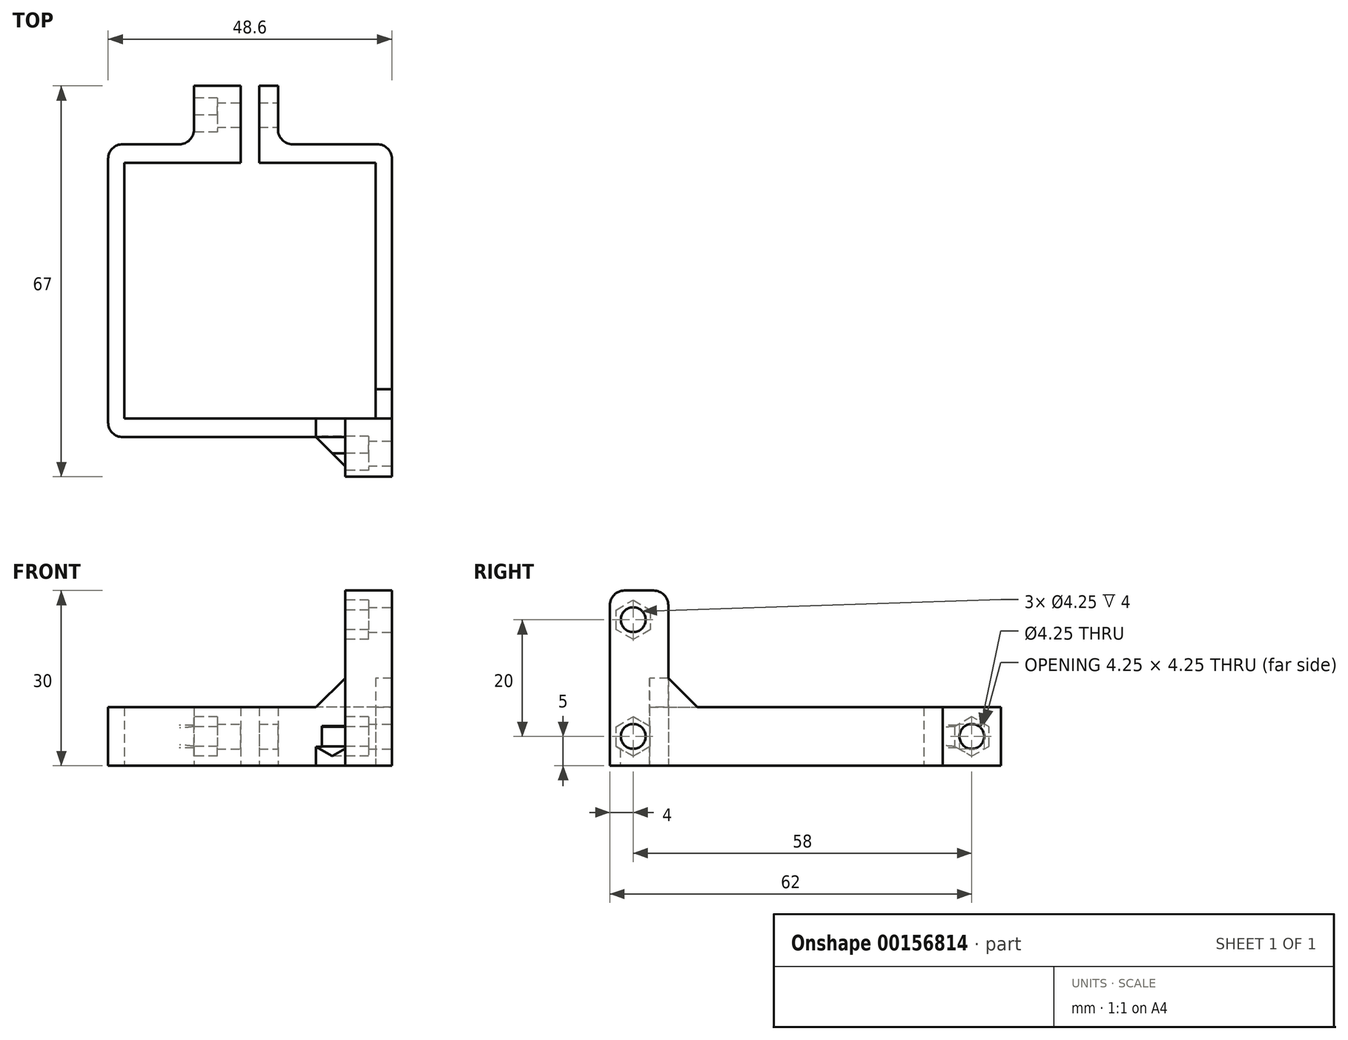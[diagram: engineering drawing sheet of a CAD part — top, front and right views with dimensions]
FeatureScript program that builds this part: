
annotation { "Feature Type Name" : "Feature", "Feature Type Description" : "" }
export const myFeature = defineFeature(function(context is Context, id is Id, definition is map)
    precondition{}
    {
        {
            var Q0;
            Q0=qCreatedBy(makeId("Top.planeOp"),FACE);
            var sketch = newSketch(context, id + "F0", { "sketchPlane" : qUnion([Q0])});
            skLineSegment(sketch, "E0.bottom", {"start": v(21.1, -21.1) * mm, "end": v(-21.1, -21.1) * mm, "construction": true});
            skLineSegment(sketch, "E0.top", {"start": v(21.1, 21.1) * mm, "end": v(-21.1, 21.1) * mm, "construction": true});
            skLineSegment(sketch, "E0.left", {"start": v(21.1, -21.1) * mm, "end": v(21.1, 21.1) * mm, "construction": true});
            skLineSegment(sketch, "E0.right", {"start": v(-21.1, -21.1) * mm, "end": v(-21.1, 21.1) * mm, "construction": true});
            skPoint(sketch, "E0.middle", {"position": v(0, 0) * mm});
            skLineSegment(sketch, "E1.bottom", {"start": v(21.5, -21.9) * mm, "end": v(-21.5, -21.9) * mm});
            skLineSegment(sketch, "E1.top", {"start": v(21.5, 21.9) * mm, "end": v(1.6, 21.9) * mm});
            skLineSegment(sketch, "E1.left", {"start": v(21.5, -21.9) * mm, "end": v(21.5, 21.9) * mm});
            skLineSegment(sketch, "E1.right", {"start": v(-21.5, -21.9) * mm, "end": v(-21.5, 21.9) * mm});
            skLineSegment(sketch, "E2.bottom", {"start": v(24.3, -25.1) * mm, "end": v(-24.3, -25.1) * mm});
            skLineSegment(sketch, "E2.top", {"start": v(24.3, 25.1) * mm, "end": v(4.8, 25.1) * mm});
            skLineSegment(sketch, "E2.left", {"start": v(24.3, -25.1) * mm, "end": v(24.3, 25.1) * mm});
            skLineSegment(sketch, "E2.right", {"start": v(-24.3, -25.1) * mm, "end": v(-24.3, 25.1) * mm});
            skLineSegment(sketch, "E3", {"start": v(-9.6, 25.1) * mm, "end": v(-9.6, 35.1) * mm});
            skLineSegment(sketch, "E4", {"start": v(-9.6, 35.1) * mm, "end": v(-1.6, 35.1) * mm});
            skLineSegment(sketch, "E5", {"start": v(-1.6, 35.1) * mm, "end": v(-1.6, 21.9) * mm});
            skLineSegment(sketch, "E6", {"start": v(1.6, 21.9) * mm, "end": v(1.6, 35.1) * mm});
            skLineSegment(sketch, "E7", {"start": v(1.6, 35.1) * mm, "end": v(4.8, 35.1) * mm});
            skLineSegment(sketch, "E8", {"start": v(4.8, 35.1) * mm, "end": v(4.8, 25.1) * mm});
            skLineSegment(sketch, "E9.trimOffspring", {"start": v(-9.6, 25.1) * mm, "end": v(-24.3, 25.1) * mm});
            skLineSegment(sketch, "E10.trimOffspring", {"start": v(-1.6, 21.9) * mm, "end": v(-21.5, 21.9) * mm});
            skSolve(sketch);
        }
        {
            var Q0;
            Q0=qSketchRegion(id+"F0",true);
            extrude(context, id + "F1", {"entities" : qUnion([Q0]), "depth" : 10 * mm});
        }
        {
            var Q0;
            Q0=makeQuery(id+"F1.opExtrude","SWEPT_FACE",FACE,{"disambiguationData":[OSD([sQuery(id+"F0.wireOp",EDGE,"E8")])]});
            var sketch = newSketch(context, id + "F2", { "sketchPlane" : qUnion([Q0])});
            skCircle(sketch, "E11", {"center": v(30.1, 5) * mm, "radius": 2.12 * mm});
            skSolve(sketch);
        }
        {
            var Q0;
            Q0=qSketchRegion(id+"F2",true);
            extrude(context, id + "F3", {"entities" : qUnion([Q0]), "operationType" : NewBodyOperationType.REMOVE, "endBound" : BoundingType.THROUGH_ALL, "oppositeDirection" : true, "depth" : 25 * mm});
        }
        {
            var Q0;
            Q0=qCreatedBy(makeId("Top.planeOp"),FACE);
            var sketch = newSketch(context, id + "F4", { "sketchPlane" : qUnion([Q0])});
            skLineSegment(sketch, "E12.bottom", {"start": v(16.3, -21.9) * mm, "end": v(24.3, -21.9) * mm});
            skLineSegment(sketch, "E12.top", {"start": v(16.3, -31.9) * mm, "end": v(24.3, -31.9) * mm});
            skLineSegment(sketch, "E12.left", {"start": v(16.3, -21.9) * mm, "end": v(16.3, -31.9) * mm});
            skLineSegment(sketch, "E12.right", {"start": v(24.3, -21.9) * mm, "end": v(24.3, -31.9) * mm});
            skLineSegment(sketch, "E13.bottom", {"start": v(-24.3, 21.9) * mm, "end": v(-14.3, 21.9) * mm, "construction": true});
            skLineSegment(sketch, "E13.top", {"start": v(-24.3, 29.9) * mm, "end": v(-14.3, 29.9) * mm, "construction": true});
            skLineSegment(sketch, "E13.left", {"start": v(-24.3, 21.9) * mm, "end": v(-24.3, 29.9) * mm, "construction": true});
            skLineSegment(sketch, "E13.right", {"start": v(-14.3, 21.9) * mm, "end": v(-14.3, 29.9) * mm, "construction": true});
            skSolve(sketch);
        }
        {
            var Q0;
            Q0=qSketchRegion(id+"F4",true);
            extrude(context, id + "F5", {"entities" : qUnion([Q0]), "operationType" : NewBodyOperationType.ADD, "depth" : 30 * mm});
        }
        {
            var Q0;
            Q0=makeQuery(id+"F5.boolean.opBoolean","MERGE",FACE,{"derivedFrom":[makeQuery(id+"F1.opExtrude","SWEPT_FACE",FACE,{"disambiguationData":[OSD([sQuery(id+"F0.wireOp",EDGE,"E2.left")])]}),makeQuery(id+"F5.opExtrude","SWEPT_FACE",FACE,{"disambiguationData":[OSD([sQuery(id+"F4.wireOp",EDGE,"E12.right")])]})]});
            var sketch = newSketch(context, id + "F6", { "sketchPlane" : qUnion([Q0])});
            skCircle(sketch, "E14", {"center": v(-27.9, 25) * mm, "radius": 2.12 * mm});
            skCircle(sketch, "E15", {"center": v(-27.9, 5) * mm, "radius": 2.12 * mm});
            skSolve(sketch);
        }
        {
            var Q0;
            Q0=qSketchRegion(id+"F6",true);
            extrude(context, id + "F7", {"entities" : qUnion([Q0]), "operationType" : NewBodyOperationType.REMOVE, "endBound" : BoundingType.THROUGH_ALL, "oppositeDirection" : true, "depth" : 25 * mm});
        }
        {
            var Q0;
            Q0=makeQuery(id+"F5.opExtrude","SWEPT_FACE",FACE,{"disambiguationData":[OSD([sQuery(id+"F4.wireOp",EDGE,"E12.left")])]});
            var sketch = newSketch(context, id + "F8", { "sketchPlane" : qUnion([Q0])});
            skCircle(sketch, "E16.cCircle", {"center": v(27.9, 25) * mm, "radius": 2.93 * mm, "construction": true});
            skLineSegment(sketch, "E16.0", {"start": v(30.82, 26.69) * mm, "end": v(30.82, 23.31) * mm});
            skLineSegment(sketch, "E16.1", {"start": v(30.82, 23.31) * mm, "end": v(27.9, 21.62) * mm});
            skLineSegment(sketch, "E16.2", {"start": v(27.9, 21.62) * mm, "end": v(24.98, 23.31) * mm});
            skLineSegment(sketch, "E16.3", {"start": v(24.97, 23.31) * mm, "end": v(24.97, 26.69) * mm});
            skLineSegment(sketch, "E16.4", {"start": v(24.98, 26.69) * mm, "end": v(27.9, 28.38) * mm});
            skLineSegment(sketch, "E16.5", {"start": v(27.9, 28.38) * mm, "end": v(30.82, 26.69) * mm});
            skPoint(sketch, "E16.0.midPoint", {"position": v(30.82, 25) * mm});
            skCircle(sketch, "E17.cCircle", {"center": v(27.9, 5) * mm, "radius": 2.93 * mm, "construction": true});
            skLineSegment(sketch, "E17.0", {"start": v(30.82, 6.69) * mm, "end": v(30.82, 3.31) * mm});
            skLineSegment(sketch, "E17.1", {"start": v(30.83, 3.31) * mm, "end": v(27.9, 1.62) * mm});
            skLineSegment(sketch, "E17.2", {"start": v(27.9, 1.62) * mm, "end": v(24.98, 3.31) * mm});
            skLineSegment(sketch, "E17.3", {"start": v(24.97, 3.31) * mm, "end": v(24.97, 6.69) * mm});
            skLineSegment(sketch, "E17.4", {"start": v(24.97, 6.69) * mm, "end": v(27.9, 8.38) * mm});
            skLineSegment(sketch, "E17.5", {"start": v(27.9, 8.38) * mm, "end": v(30.82, 6.69) * mm});
            skPoint(sketch, "E17.0.midPoint", {"position": v(30.82, 5) * mm});
            skSolve(sketch);
        }
        {
            var Q0;
            Q0=qSketchRegion(id+"F8",true);
            extrude(context, id + "F9", {"entities" : qUnion([Q0]), "operationType" : NewBodyOperationType.REMOVE, "endBound" : BoundingType.SYMMETRIC, "oppositeDirection" : true, "depth" : 8 * mm});
        }
        {
            var Q0;
            Q0=makeQuery(id+"F5.boolean.opBoolean","INTERSECT",EDGE,{"derivedFrom":[makeQuery(id+"F1.opExtrude","CAP_FACE",FACE,{"disambiguationData":[OSD([sQuery(id+"F0.wireOp",EDGE,"E1.bottom"),sQuery(id+"F0.wireOp",EDGE,"E1.top"),sQuery(id+"F0.wireOp",EDGE,"E1.left"),sQuery(id+"F0.wireOp",EDGE,"E1.right"),sQuery(id+"F0.wireOp",EDGE,"E2.bottom"),sQuery(id+"F0.wireOp",EDGE,"E2.top"),sQuery(id+"F0.wireOp",EDGE,"E2.left"),sQuery(id+"F0.wireOp",EDGE,"E2.right"),sQuery(id+"F0.wireOp",EDGE,"E3"),sQuery(id+"F0.wireOp",EDGE,"E4"),sQuery(id+"F0.wireOp",EDGE,"E5"),sQuery(id+"F0.wireOp",EDGE,"E6"),sQuery(id+"F0.wireOp",EDGE,"E7"),sQuery(id+"F0.wireOp",EDGE,"E8"),sQuery(id+"F0.wireOp",EDGE,"E9.trimOffspring"),sQuery(id+"F0.wireOp",EDGE,"E10.trimOffspring")])],"isStart":false}),makeQuery(id+"F5.opExtrude","SWEPT_FACE",FACE,{"disambiguationData":[OSD([sQuery(id+"F4.wireOp",EDGE,"E12.bottom")])]})]});
            var Q1;
            Q1=makeQuery(id+"F5.boolean.opBoolean","INTERSECT",EDGE,{"derivedFrom":[makeQuery(id+"F1.opExtrude","CAP_FACE",FACE,{"disambiguationData":[OSD([sQuery(id+"F0.wireOp",EDGE,"E1.bottom"),sQuery(id+"F0.wireOp",EDGE,"E1.top"),sQuery(id+"F0.wireOp",EDGE,"E1.left"),sQuery(id+"F0.wireOp",EDGE,"E1.right"),sQuery(id+"F0.wireOp",EDGE,"E2.bottom"),sQuery(id+"F0.wireOp",EDGE,"E2.top"),sQuery(id+"F0.wireOp",EDGE,"E2.left"),sQuery(id+"F0.wireOp",EDGE,"E2.right"),sQuery(id+"F0.wireOp",EDGE,"E3"),sQuery(id+"F0.wireOp",EDGE,"E4"),sQuery(id+"F0.wireOp",EDGE,"E5"),sQuery(id+"F0.wireOp",EDGE,"E6"),sQuery(id+"F0.wireOp",EDGE,"E7"),sQuery(id+"F0.wireOp",EDGE,"E8"),sQuery(id+"F0.wireOp",EDGE,"E9.trimOffspring"),sQuery(id+"F0.wireOp",EDGE,"E10.trimOffspring")])],"isStart":false}),makeQuery(id+"F5.opExtrude","SWEPT_FACE",FACE,{"disambiguationData":[OSD([sQuery(id+"F4.wireOp",EDGE,"E12.left")])]})]});
            var Q2;
            {var subQ0=sQuery(id+"F4.wireOp",EDGE,"E12.left");var subQ1=makeQuery(id+"F5.opExtrude","SWEPT_FACE",FACE,{"disambiguationData":[OSD([subQ0])]});var subQ2=sQuery(id+"F0.wireOp",EDGE,"E2.bottom");var subQ3=makeQuery(id+"F1.opExtrude","SWEPT_FACE",FACE,{"disambiguationData":[OSD([subQ2])]});var subQ4=sQuery(id+"F8.wireOp",EDGE,"E17.2");Q2=makeQuery(id+"F9.boolean.opBoolean","SPLIT",EDGE,{"disambiguationData":[TD([makeQuery(id+"F1.opExtrude","CAP_FACE",FACE,{"disambiguationData":[OSD([sQuery(id+"F0.wireOp",EDGE,"E1.bottom"),sQuery(id+"F0.wireOp",EDGE,"E1.top"),sQuery(id+"F0.wireOp",EDGE,"E1.left"),sQuery(id+"F0.wireOp",EDGE,"E1.right"),subQ2,sQuery(id+"F0.wireOp",EDGE,"E2.top"),sQuery(id+"F0.wireOp",EDGE,"E2.left"),sQuery(id+"F0.wireOp",EDGE,"E2.right"),sQuery(id+"F0.wireOp",EDGE,"E3"),sQuery(id+"F0.wireOp",EDGE,"E4"),sQuery(id+"F0.wireOp",EDGE,"E5"),sQuery(id+"F0.wireOp",EDGE,"E6"),sQuery(id+"F0.wireOp",EDGE,"E7"),sQuery(id+"F0.wireOp",EDGE,"E8"),sQuery(id+"F0.wireOp",EDGE,"E9.trimOffspring"),sQuery(id+"F0.wireOp",EDGE,"E10.trimOffspring")])],"isStart":true}),subQ3,makeQuery(id+"F5.opExtrude","CAP_FACE",FACE,{"disambiguationData":[OSD([sQuery(id+"F4.wireOp",EDGE,"E12.bottom"),sQuery(id+"F4.wireOp",EDGE,"E12.top"),subQ0,sQuery(id+"F4.wireOp",EDGE,"E12.right")])],"isStart":true}),subQ1,makeQuery(id+"F9.opExtrude","CAP_FACE",FACE,{"disambiguationData":[OSD([sQuery(id+"F8.wireOp",EDGE,"E17.0"),sQuery(id+"F8.wireOp",EDGE,"E17.1"),subQ4,sQuery(id+"F8.wireOp",EDGE,"E17.3"),sQuery(id+"F8.wireOp",EDGE,"E17.4"),sQuery(id+"F8.wireOp",EDGE,"E17.5")])],"isStart":true}),makeQuery(id+"F9.opExtrude","SWEPT_FACE",FACE,{"disambiguationData":[OSD([subQ4])]})])],"derivedFrom":makeQuery(id+"F5.boolean.opBoolean","INTERSECT",EDGE,{"derivedFrom":[subQ3,subQ1]})});}
            chamfer(context, id + "F10", {"entities" : qUnion([Q0, Q1, Q2]), "width" : 5 * mm, "tangentPropagation" : true});
        }
        {
            var Q0;
            Q0=makeQuery(id+"F1.opExtrude","SWEPT_FACE",FACE,{"disambiguationData":[OSD([sQuery(id+"F0.wireOp",EDGE,"E3")])]});
            var sketch = newSketch(context, id + "F11", { "sketchPlane" : qUnion([Q0])});
            skCircle(sketch, "E18.cCircle", {"center": v(-30.1, 5) * mm, "radius": 2.93 * mm, "construction": true});
            skLineSegment(sketch, "E18.0", {"start": v(-27.17, 6.69) * mm, "end": v(-27.17, 3.31) * mm});
            skLineSegment(sketch, "E18.1", {"start": v(-27.17, 3.31) * mm, "end": v(-30.1, 1.62) * mm});
            skLineSegment(sketch, "E18.2", {"start": v(-30.1, 1.62) * mm, "end": v(-33.02, 3.31) * mm});
            skLineSegment(sketch, "E18.3", {"start": v(-33.02, 3.31) * mm, "end": v(-33.02, 6.69) * mm});
            skLineSegment(sketch, "E18.4", {"start": v(-33.02, 6.69) * mm, "end": v(-30.1, 8.38) * mm});
            skLineSegment(sketch, "E18.5", {"start": v(-30.1, 8.38) * mm, "end": v(-27.17, 6.69) * mm});
            skPoint(sketch, "E18.0.midPoint", {"position": v(-27.17, 5) * mm});
            skSolve(sketch);
        }
        {
            var Q0;
            Q0=qSketchRegion(id+"F11",true);
            extrude(context, id + "F12", {"entities" : qUnion([Q0]), "operationType" : NewBodyOperationType.REMOVE, "oppositeDirection" : true, "depth" : 4 * mm});
        }
        {
            var Q0;
            Q0=makeQuery(id+"F1.opExtrude","SWEPT_EDGE",EDGE,{"disambiguationData":[OSD([sQuery(id+"F0.wireOp",EDGE,"E2.right"),sQuery(id+"F0.wireOp",EDGE,"E9.trimOffspring")])]});
            var Q1;
            Q1=makeQuery(id+"F1.opExtrude","SWEPT_EDGE",EDGE,{"disambiguationData":[OSD([sQuery(id+"F0.wireOp",EDGE,"E2.bottom"),sQuery(id+"F0.wireOp",EDGE,"E2.right")])]});
            var Q2;
            Q2=makeQuery(id+"F1.opExtrude","SWEPT_EDGE",EDGE,{"disambiguationData":[OSD([sQuery(id+"F0.wireOp",EDGE,"E2.top"),sQuery(id+"F0.wireOp",EDGE,"E2.left")])]});
            var Q3;
            Q3=makeQuery(id+"F5.opExtrude","SWEPT_EDGE",EDGE,{"disambiguationData":[OSD([sQuery(id+"F4.wireOp",EDGE,"E13.top"),sQuery(id+"F4.wireOp",EDGE,"E13.right")])]});
            var Q4;
            Q4=makeQuery(id+"F1.opExtrude","SWEPT_EDGE",EDGE,{"disambiguationData":[OSD([sQuery(id+"F0.wireOp",EDGE,"E3"),sQuery(id+"F0.wireOp",EDGE,"E9.trimOffspring")])]});
            var Q5;
            Q5=makeQuery(id+"F1.opExtrude","SWEPT_EDGE",EDGE,{"disambiguationData":[OSD([sQuery(id+"F0.wireOp",EDGE,"E2.top"),sQuery(id+"F0.wireOp",EDGE,"E8")])]});
            fillet(context, id + "F13", {"entities" : qUnion([Q0, Q1, Q2, Q3, Q4, Q5]), "radius" : 2.5 * mm, "tangentPropagation" : true, "allowEdgeOverflow" : false});
        }
        {
            var Q0;
            Q0=makeQuery(id+"F5.opExtrude","CAP_EDGE",EDGE,{"disambiguationData":[OSD([sQuery(id+"F4.wireOp",EDGE,"E12.top")])],"isStart":false});
            var Q1;
            Q1=makeQuery(id+"F5.opExtrude","CAP_EDGE",EDGE,{"disambiguationData":[OSD([sQuery(id+"F4.wireOp",EDGE,"E12.bottom")])],"isStart":false});
            fillet(context, id + "F14", {"entities" : qUnion([Q0, Q1]), "radius" : 2.5 * mm, "tangentPropagation" : true, "allowEdgeOverflow" : false});
        }
    });
